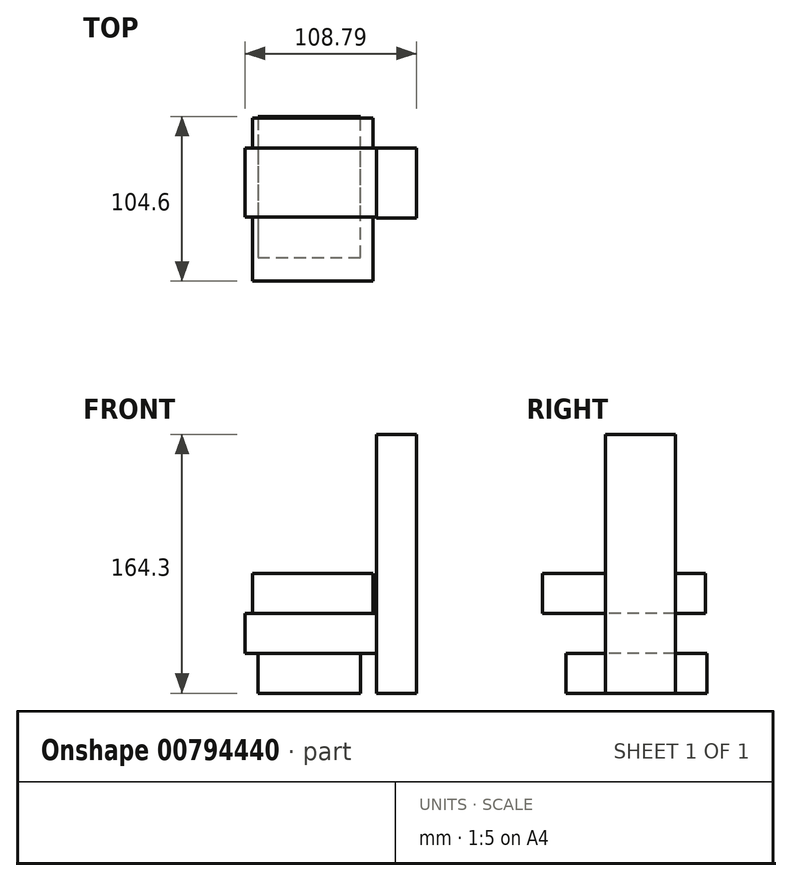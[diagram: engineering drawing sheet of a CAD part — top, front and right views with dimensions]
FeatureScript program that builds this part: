
annotation { "Feature Type Name" : "Feature", "Feature Type Description" : "" }
export const myFeature = defineFeature(function(context is Context, id is Id, definition is map)
    precondition{}
    {
        {
            var Q0;
            Q0=qCreatedBy(makeId("Top.planeOp"),FACE);
            var sketch = newSketch(context, id + "F0", { "sketchPlane" : qUnion([Q0])});
            skLineSegment(sketch, "E0", {"start": v(-19.74, 43.1) * mm, "end": v(-19.74, -46.53) * mm});
            skLineSegment(sketch, "E1", {"start": v(-19.74, -46.53) * mm, "end": v(45.48, -46.53) * mm});
            skLineSegment(sketch, "E2", {"start": v(45.48, -46.53) * mm, "end": v(45.48, 43.1) * mm});
            skLineSegment(sketch, "E3", {"start": v(45.48, 43.1) * mm, "end": v(-19.74, 43.1) * mm});
            skSolve(sketch);
        }
        {
            var Q0;
            Q0=makeQuery(id+"F0.imprint","IMPRINT",FACE,{"disambiguationData":[TD([[makeQuery(id+"F0.imprint","IMPRINT",EDGE,{"derivedFrom":sQuery(id+"F0.wireOp",EDGE,"E0")}),1.0]])]});
            extrude(context, id + "F1", {"entities" : qUnion([Q0]), "depth" : 25.4 * mm, "offsetDistance" : 25.4 * mm});
        }
        {
            var Q0;
            Q0=makeQuery(id+"F1.opExtrude","CAP_FACE",FACE,{"disambiguationData":[OSD([sQuery(id+"F0.wireOp",EDGE,"E0"),sQuery(id+"F0.wireOp",EDGE,"E1"),sQuery(id+"F0.wireOp",EDGE,"E2"),sQuery(id+"F0.wireOp",EDGE,"E3")])],"isStart":false});
            var sketch = newSketch(context, id + "F2", { "sketchPlane" : qUnion([Q0])});
            skLineSegment(sketch, "E4.bottom", {"start": v(-27.87, 22.9) * mm, "end": v(55.52, 22.9) * mm});
            skLineSegment(sketch, "E4.top", {"start": v(-27.87, -21.02) * mm, "end": v(55.52, -21.02) * mm});
            skLineSegment(sketch, "E4.left", {"start": v(-27.87, 22.9) * mm, "end": v(-27.87, -21.02) * mm});
            skLineSegment(sketch, "E4.right", {"start": v(55.52, 22.9) * mm, "end": v(55.52, -21.02) * mm});
            skSolve(sketch);
        }
        {
            var Q0;
            Q0 = qSketchRegion(id + "F2", true);
            var Q1;
            {var subQ0=sQuery(id+"F2.wireOp",EDGE,"E4.bottom");var subQ1=makeQuery(id+"F1.opExtrude","CAP_EDGE",EDGE,{"disambiguationData":[OSD([sQuery(id+"F0.wireOp",EDGE,"E0")])],"isStart":false});var subQ2=makeQuery(id+"F2.imprint","INTERSECT",VERTEX,{"derivedFrom":[subQ1,subQ0]});Q1=makeQuery(id+"F2.imprint","IMPRINT",FACE,{"disambiguationData":[TD([[makeQuery(id+"F2.imprint","IMPRINT",EDGE,{"disambiguationData":[TD([[subQ2,-1.0]])],"derivedFrom":subQ0}),-1.0]])]});}
            extrude(context, id + "F3", {"entities" : qUnion([Q0, Q1]), "operationType" : NewBodyOperationType.ADD, "depth" : 25.4 * mm, "offsetDistance" : 25.4 * mm});
        }
        {
            var Q0;
            Q0=makeQuery(id+"F3.opExtrude","CAP_FACE",FACE,{"disambiguationData":[OSD([sQuery(id+"F2.wireOp",EDGE,"E4.bottom"),sQuery(id+"F2.wireOp",EDGE,"E4.top"),sQuery(id+"F2.wireOp",EDGE,"E4.left"),sQuery(id+"F2.wireOp",EDGE,"E4.right")])],"isStart":false});
            var sketch = newSketch(context, id + "F4", { "sketchPlane" : qUnion([Q0])});
            skLineSegment(sketch, "E5.bottom", {"start": v(-23.08, 42.01) * mm, "end": v(53.47, 42.01) * mm});
            skLineSegment(sketch, "E5.top", {"start": v(-23.08, -61.5) * mm, "end": v(53.47, -61.5) * mm});
            skLineSegment(sketch, "E5.left", {"start": v(-23.08, 42.01) * mm, "end": v(-23.08, -61.5) * mm});
            skLineSegment(sketch, "E5.right", {"start": v(53.47, 42.01) * mm, "end": v(53.47, -61.5) * mm});
            skSolve(sketch);
        }
        {
            var Q0;
            {var subQ0=sQuery(id+"F4.wireOp",EDGE,"E5.bottom");Q0=makeQuery(id+"F4.imprint","IMPRINT",FACE,{"disambiguationData":[TD([[makeQuery(id+"F4.imprint","IMPRINT",EDGE,{"derivedFrom":subQ0}),-1.0]])]});}
            var Q1;
            {var subQ0=sQuery(id+"F4.wireOp",EDGE,"E5.top");Q1=makeQuery(id+"F4.imprint","IMPRINT",FACE,{"disambiguationData":[TD([[makeQuery(id+"F4.imprint","IMPRINT",EDGE,{"derivedFrom":subQ0}),1.0]])]});}
            extrude(context, id + "F5", {"entities" : qUnion([Q0, Q1]), "depth" : 25.4 * mm, "offsetDistance" : 25.4 * mm});
        }
        {
            var Q0;
            Q0=makeQuery(id+"F3.opExtrude","SWEPT_FACE",FACE,{"disambiguationData":[OSD([sQuery(id+"F2.wireOp",EDGE,"E4.right")])]});
            var sketch = newSketch(context, id + "F6", { "sketchPlane" : qUnion([Q0])});
            skLineSegment(sketch, "E6.bottom", {"start": v(-21.44, 164.3) * mm, "end": v(22.9, 164.3) * mm});
            skLineSegment(sketch, "E6.top", {"start": v(-21.44, 0) * mm, "end": v(22.9, 0) * mm});
            skLineSegment(sketch, "E6.left", {"start": v(-21.44, 164.3) * mm, "end": v(-21.44, 0) * mm});
            skLineSegment(sketch, "E6.right", {"start": v(22.9, 164.3) * mm, "end": v(22.9, 0) * mm});
            skSolve(sketch);
        }
        {
            var Q0;
            Q0 = qSketchRegion(id + "F6", true);
            extrude(context, id + "F7", {"entities" : qUnion([Q0]), "operationType" : NewBodyOperationType.ADD, "depth" : 25.4 * mm, "offsetDistance" : 25.4 * mm});
        }
    });
